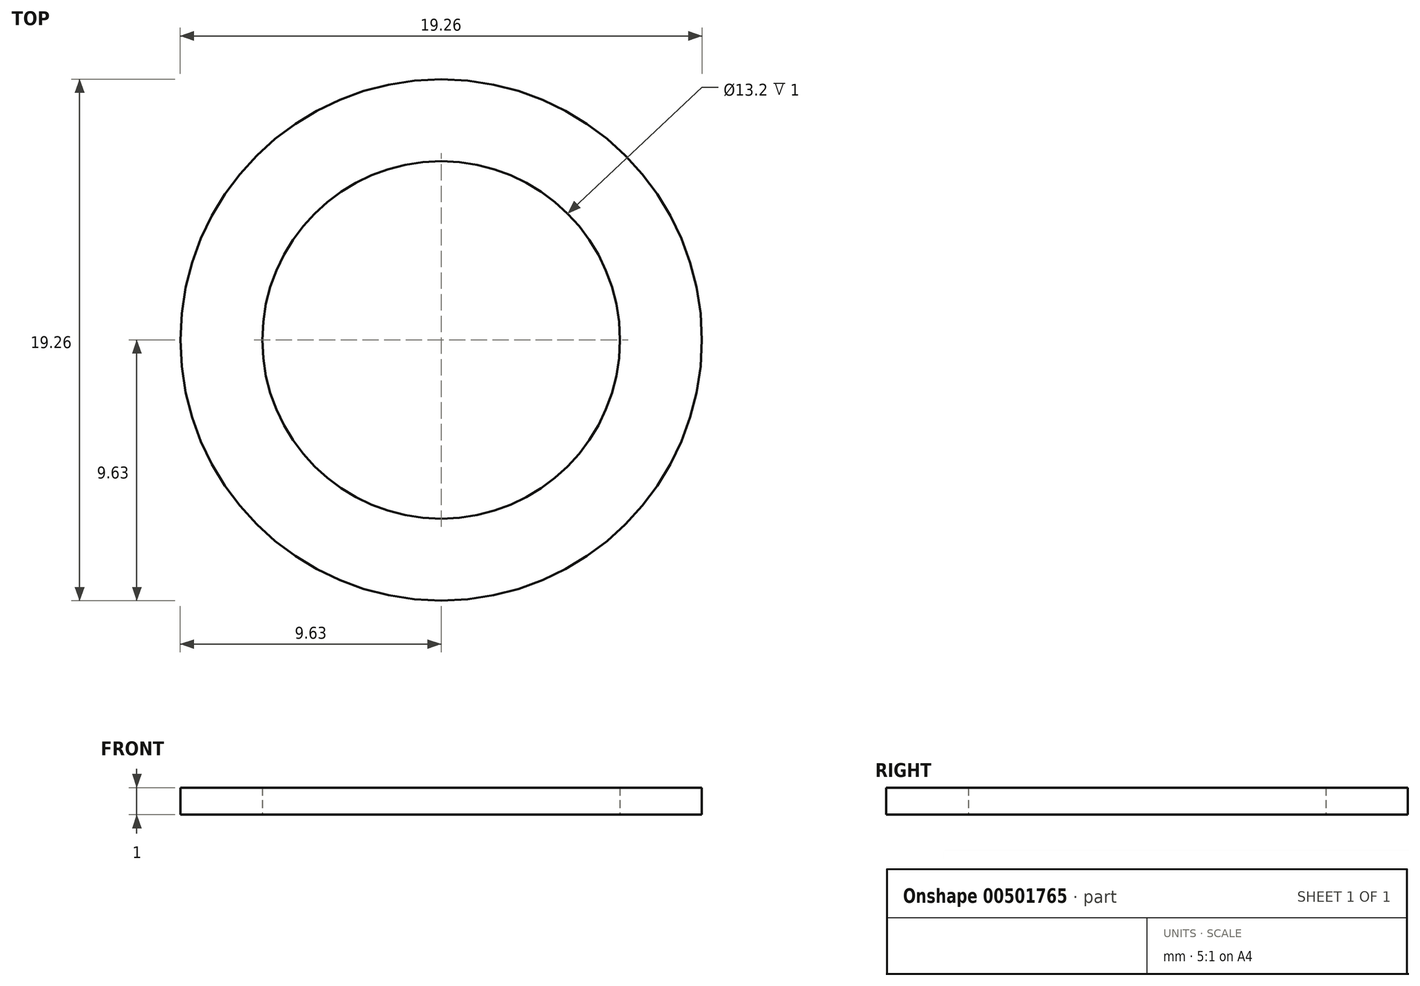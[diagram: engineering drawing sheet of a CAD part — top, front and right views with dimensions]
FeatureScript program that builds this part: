
annotation { "Feature Type Name" : "Feature", "Feature Type Description" : "" }
export const myFeature = defineFeature(function(context is Context, id is Id, definition is map)
    precondition{}
    {
        {
            var Q0;
            Q0=qCreatedBy(makeId("Top.planeOp"),FACE);
            var sketch = newSketch(context, id + "F0", { "sketchPlane" : qUnion([Q0])});
            skCircle(sketch, "E0", {"center": v(0, 0) * mm, "radius": 9.62 * mm});
            skCircle(sketch, "E1", {"center": v(0, 0) * mm, "radius": 6.6 * mm});
            skSolve(sketch);
        }
        {
            var Q0;
            Q0 = qSketchRegion(id + "F0", true);
            extrude(context, id + "F1", {"entities" : qUnion([Q0]), "depth" : 1 * mm});
        }
    });
